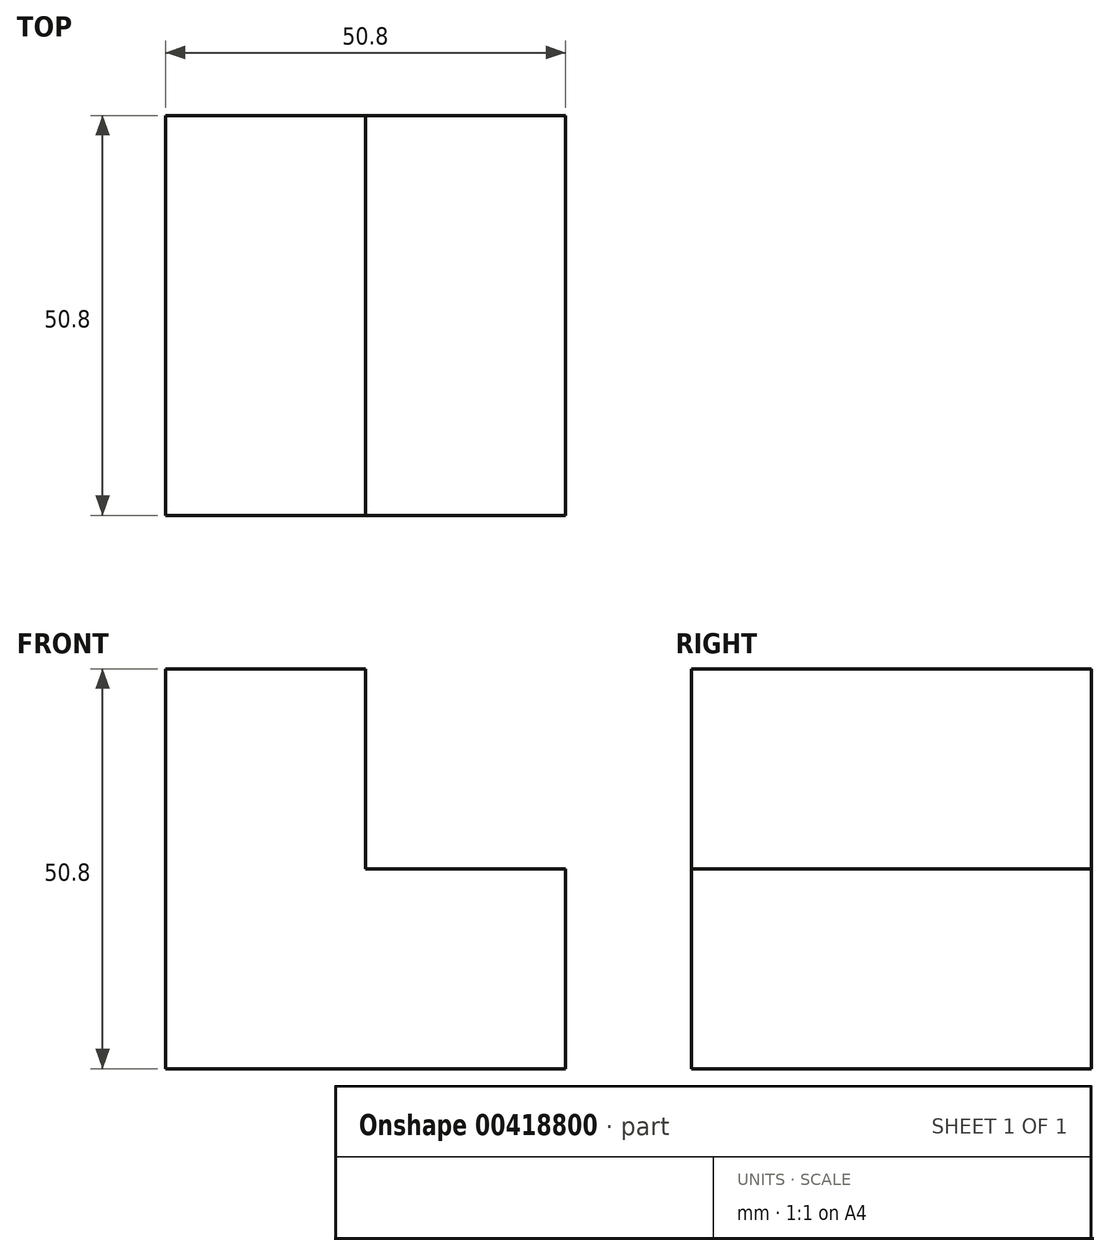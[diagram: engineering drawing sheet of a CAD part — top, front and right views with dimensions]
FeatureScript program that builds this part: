
annotation { "Feature Type Name" : "Feature", "Feature Type Description" : "" }
export const myFeature = defineFeature(function(context is Context, id is Id, definition is map)
    precondition{}
    {
        {
            var Q0;
            Q0=qCreatedBy(makeId("Front.planeOp"),FACE);
            var sketch = newSketch(context, id + "F0", { "sketchPlane" : qUnion([Q0])});
            skLineSegment(sketch, "E0", {"start": v(-42.77, 17) * mm, "end": v(-42.77, 67.8) * mm});
            skLineSegment(sketch, "E1", {"start": v(-42.77, 67.8) * mm, "end": v(-17.37, 67.8) * mm});
            skLineSegment(sketch, "E2", {"start": v(-17.37, 67.8) * mm, "end": v(-17.37, 42.4) * mm});
            skLineSegment(sketch, "E3", {"start": v(-17.37, 42.4) * mm, "end": v(8.03, 42.4) * mm});
            skLineSegment(sketch, "E4", {"start": v(8.03, 42.4) * mm, "end": v(8.03, 17) * mm});
            skLineSegment(sketch, "E5", {"start": v(8.03, 17) * mm, "end": v(-42.77, 17) * mm});
            skSolve(sketch);
        }
        {
            var Q0;
            Q0 = qSketchRegion(id + "F0", true);
            extrude(context, id + "F1", {"entities" : qUnion([Q0]), "depth" : 50.8 * mm});
        }
    });
